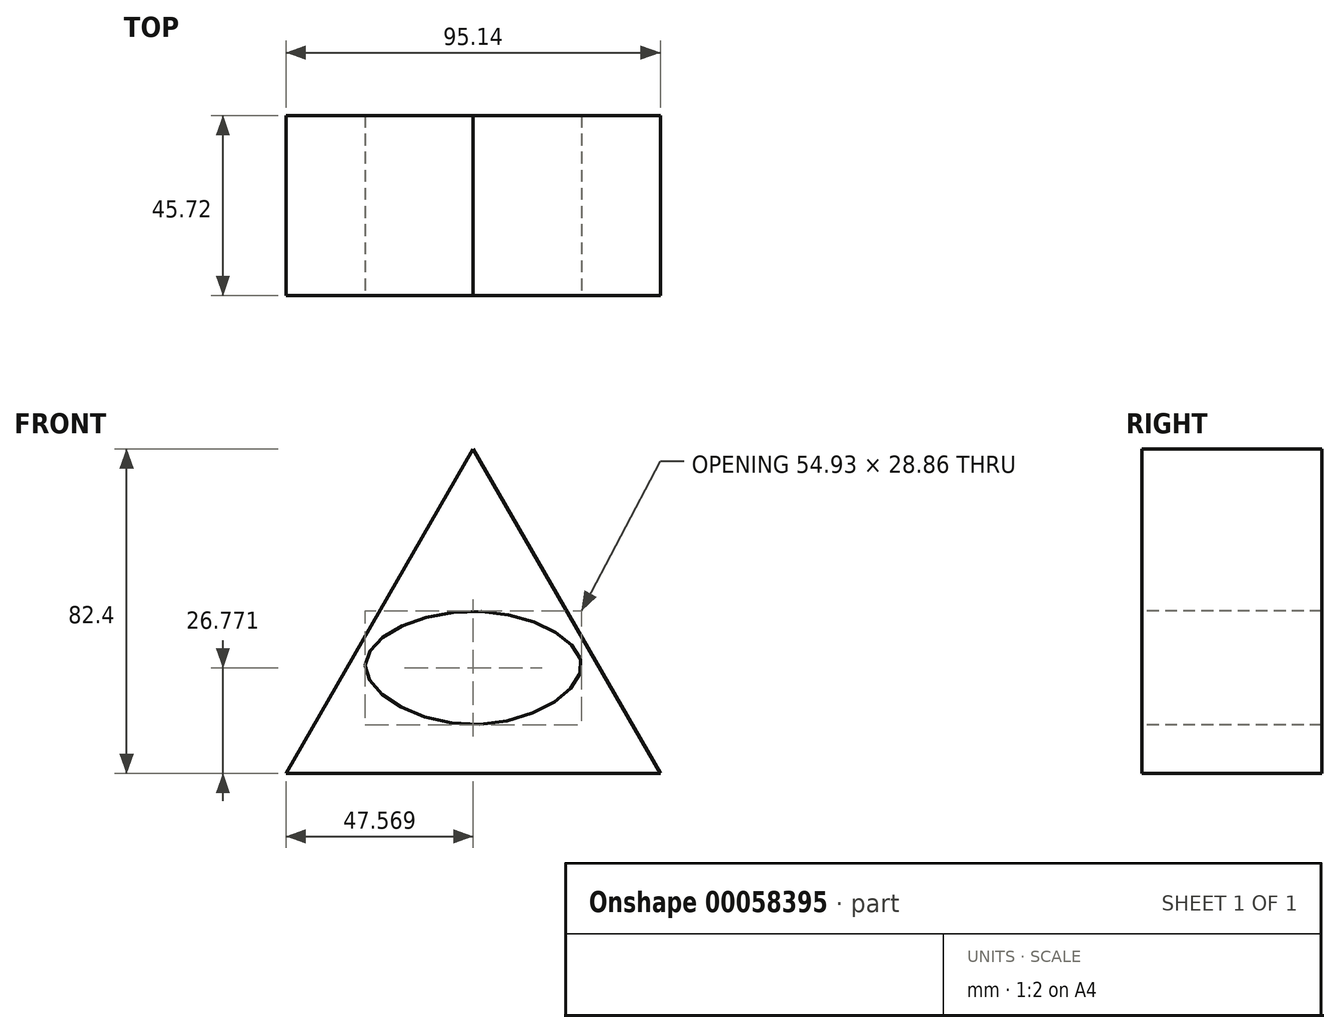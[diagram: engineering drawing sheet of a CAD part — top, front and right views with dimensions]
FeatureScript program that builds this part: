
annotation { "Feature Type Name" : "Feature", "Feature Type Description" : "" }
export const myFeature = defineFeature(function(context is Context, id is Id, definition is map)
    precondition{}
    {
        {
            var Q0;
            Q0=qCreatedBy(makeId("Front.planeOp"),FACE);
            var sketch = newSketch(context, id + "F0", { "sketchPlane" : qUnion([Q0])});
            skLineSegment(sketch, "E0.0", {"start": v(0, 54.93) * mm, "end": v(47.57, -27.47) * mm});
            skLineSegment(sketch, "E0.1", {"start": v(47.57, -27.47) * mm, "end": v(-47.57, -27.47) * mm});
            skLineSegment(sketch, "E0.2", {"start": v(-47.57, -27.47) * mm, "end": v(0, 54.93) * mm});
            skPoint(sketch, "E0.0.midPoint", {"position": v(23.79, 13.73) * mm});
            skPoint(sketch, "E1.1.internal.snap0", {"position": v(-23.79, 13.73) * mm});
            skFitSpline(sketch, "E1", {"points": [v(-27.47, 0) * mm, v(0, 13.73) * mm, v(27.47, 0) * mm, v(0, -15.13) * mm, v(-27.47, 0) * mm]});
            skCircle(sketch, "E2", {"center": v(0, 0) * mm, "radius": 10.54 * mm});
            skLineSegment(sketch, "E3", {"start": v(0, 10.54) * mm, "end": v(0, -10.54) * mm});
            skSolve(sketch);
        }
        {
            var Q0;
            Q0=makeQuery(id+"F0.imprint","IMPRINT",FACE,{"disambiguationData":[TD([[makeQuery(id+"F0.imprint","IMPRINT",EDGE,{"derivedFrom":sQuery(id+"F0.wireOp",EDGE,"E0.0")}),-1.0]])]});
            extrude(context, id + "F1", {"entities" : qUnion([Q0]), "depth" : 20.32 * mm});
        }
        {
            var Q0;
            Q0 = qSketchRegion(id + "F0", true);
            var Q1;
            Q1=makeQuery(id+"F1.opExtrude","CAP_FACE",FACE,{"disambiguationData":[OSD([sQuery(id+"F0.wireOp",EDGE,"E0.0"),sQuery(id+"F0.wireOp",EDGE,"E0.1"),sQuery(id+"F0.wireOp",EDGE,"E0.2"),sQuery(id+"F0.wireOp",EDGE,"E1")])],"isStart":false});
            extrude(context, id + "F2", {"entities" : qUnion([Q0, Q1]), "operationType" : NewBodyOperationType.ADD, "depth" : 25.4 * mm});
        }
    });
